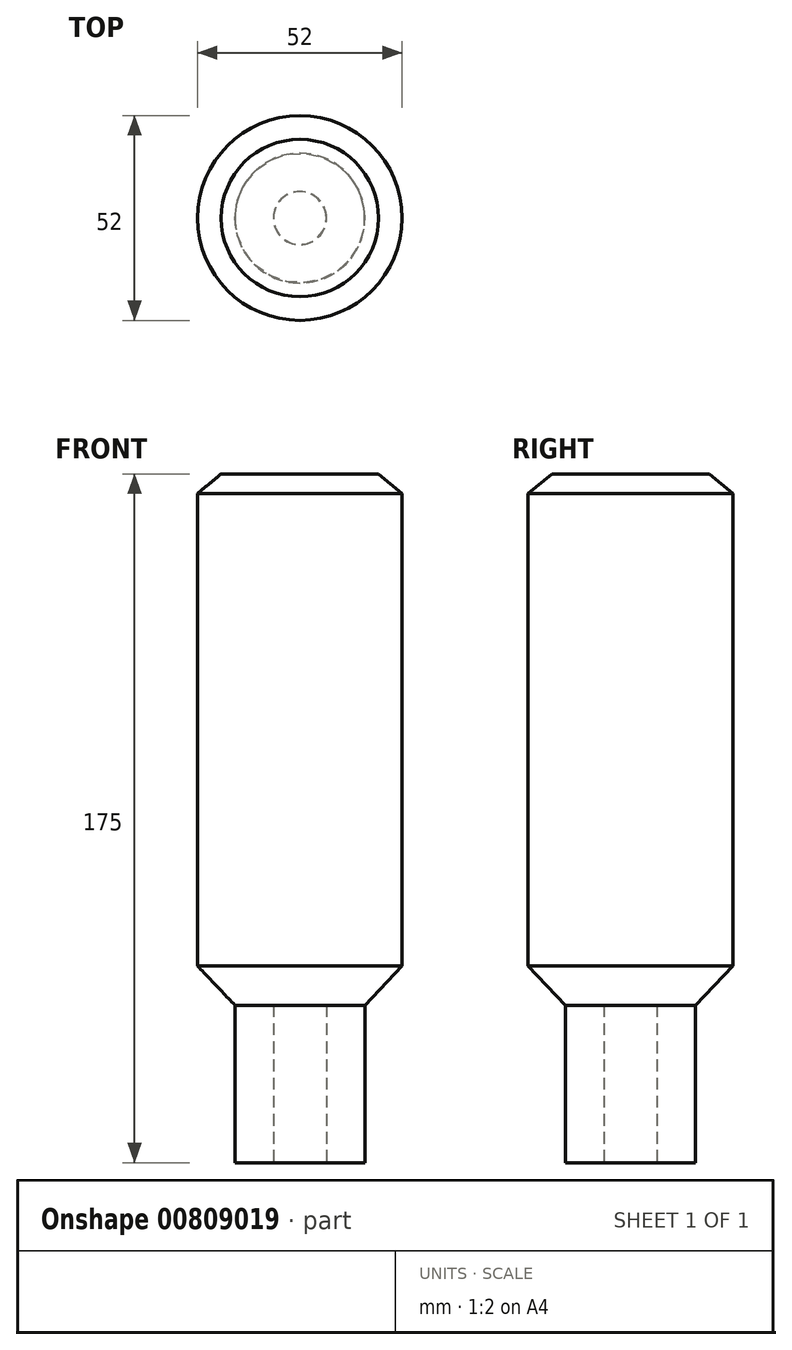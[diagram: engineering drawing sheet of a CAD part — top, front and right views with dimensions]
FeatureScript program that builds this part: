
annotation { "Feature Type Name" : "Feature", "Feature Type Description" : "" }
export const myFeature = defineFeature(function(context is Context, id is Id, definition is map)
    precondition{}
    {
        {
            var Q0;
            Q0=qCreatedBy(makeId("Top.planeOp"),FACE);
            var sketch = newSketch(context, id + "F0", { "sketchPlane" : qUnion([Q0]) });
            skCircle(sketch, "E0", {"center": v(0, 0) * mm, "radius": 16.5 * mm});
            skCircle(sketch, "E1", {"center": v(0, 0) * mm, "radius": 6.75 * mm});
            skSolve(sketch);
        }
        {
            var Q0;
            Q0=makeQuery(id+"F0.imprint","IMPRINT",FACE,{"disambiguationData":[TD([[makeQuery(id+"F0.imprint","IMPRINT",EDGE,{"derivedFrom":sQuery(id+"F0.wireOp",EDGE,"E0")}),1.0]])]});
            extrude(context, id + "F1", {"entities" : qUnion([Q0]), "depth" : 40 * mm, "offsetDistance" : 25 * mm});
        }
        {
            var Q0;
            Q0=qCreatedBy(makeId("Front.planeOp"),FACE);
            var sketch = newSketch(context, id + "F2", { "sketchPlane" : qUnion([Q0]) });
            skLineSegment(sketch, "E2", {"start": v(16.5, 40) * mm, "end": v(26, 50) * mm});
            skLineSegment(sketch, "E3", {"start": v(26, 50) * mm, "end": v(-26, 50) * mm});
            skLineSegment(sketch, "E4", {"start": v(-26, 50) * mm, "end": v(-16.5, 40) * mm});
            skLineSegment(sketch, "E5", {"start": v(-16.5, 40) * mm, "end": v(16.5, 40) * mm});
            skPoint(sketch, "E6", {"position": v(0, 40) * mm});
            skLineSegment(sketch, "E7", {"start": v(0, 40) * mm, "end": v(0, 50) * mm});
            skSolve(sketch);
        }
        {
            var Q0;
            {var subQ0=sQuery(id+"F2.wireOp",EDGE,"E2");Q0=makeQuery(id+"F2.imprint","IMPRINT",FACE,{"disambiguationData":[TD([[makeQuery(id+"F2.imprint","IMPRINT",EDGE,{"derivedFrom":subQ0}),1.0]])]});}
            var Q1;
            Q1=sQuery(id+"F2.wireOp",EDGE,"E7");
            revolve(context, id + "F3", {"operationType" : NewBodyOperationType.ADD, "surfaceOperationType" : NewSurfaceOperationType.NEW, "entities" : qUnion([Q0]), "axis" : qUnion([Q1]), "revolveType" : RevolveType.FULL});
        }
        {
            var Q0;
            Q0=makeQuery(id+"F3.opRevolve","SWEPT_FACE",FACE,{"disambiguationData":[OSD([sQuery(id+"F2.wireOp",EDGE,"E3")])]});
            var sketch = newSketch(context, id + "F4", { "sketchPlane" : qUnion([Q0]) });
            skCircle(sketch, "E8", {"center": v(0, 0) * mm, "radius": 26 * mm});
            skSolve(sketch);
        }
        {
            var Q0;
            Q0=makeQuery(id+"F4.imprint","IMPRINT",FACE,{"disambiguationData":[TD([[makeQuery(id+"F4.imprint","IMPRINT",EDGE,{"derivedFrom":sQuery(id+"F4.wireOp",EDGE,"E8")}),-1.0]])]});
            extrude(context, id + "F5", {"entities" : qUnion([Q0]), "operationType" : NewBodyOperationType.ADD, "depth" : 120 * mm, "offsetDistance" : 25 * mm});
        }
        {
            var Q0;
            Q0=qCreatedBy(makeId("Front.planeOp"),FACE);
            var sketch = newSketch(context, id + "F6", { "sketchPlane" : qUnion([Q0]) });
            skLineSegment(sketch, "E9", {"start": v(20, 175) * mm, "end": v(26, 170) * mm});
            skLineSegment(sketch, "E10", {"start": v(20, 175) * mm, "end": v(-20, 175) * mm});
            skLineSegment(sketch, "E11", {"start": v(-20, 175) * mm, "end": v(-26, 170) * mm});
            skLineSegment(sketch, "E12", {"start": v(-26, 170) * mm, "end": v(26, 170) * mm});
            skLineSegment(sketch, "E13", {"start": v(0, 170) * mm, "end": v(0, 175) * mm});
            skSolve(sketch);
        }
        {
            var Q0;
            {var subQ0=sQuery(id+"F6.wireOp",EDGE,"E11");Q0=makeQuery(id+"F6.imprint","IMPRINT",FACE,{"disambiguationData":[TD([[makeQuery(id+"F6.imprint","IMPRINT",EDGE,{"derivedFrom":subQ0}),1.0]])]});}
            var Q1;
            Q1=sQuery(id+"F6.wireOp",EDGE,"E13");
            revolve(context, id + "F7", {"operationType" : NewBodyOperationType.ADD, "surfaceOperationType" : NewSurfaceOperationType.NEW, "entities" : qUnion([Q0]), "axis" : qUnion([Q1]), "revolveType" : RevolveType.FULL});
        }
    });
